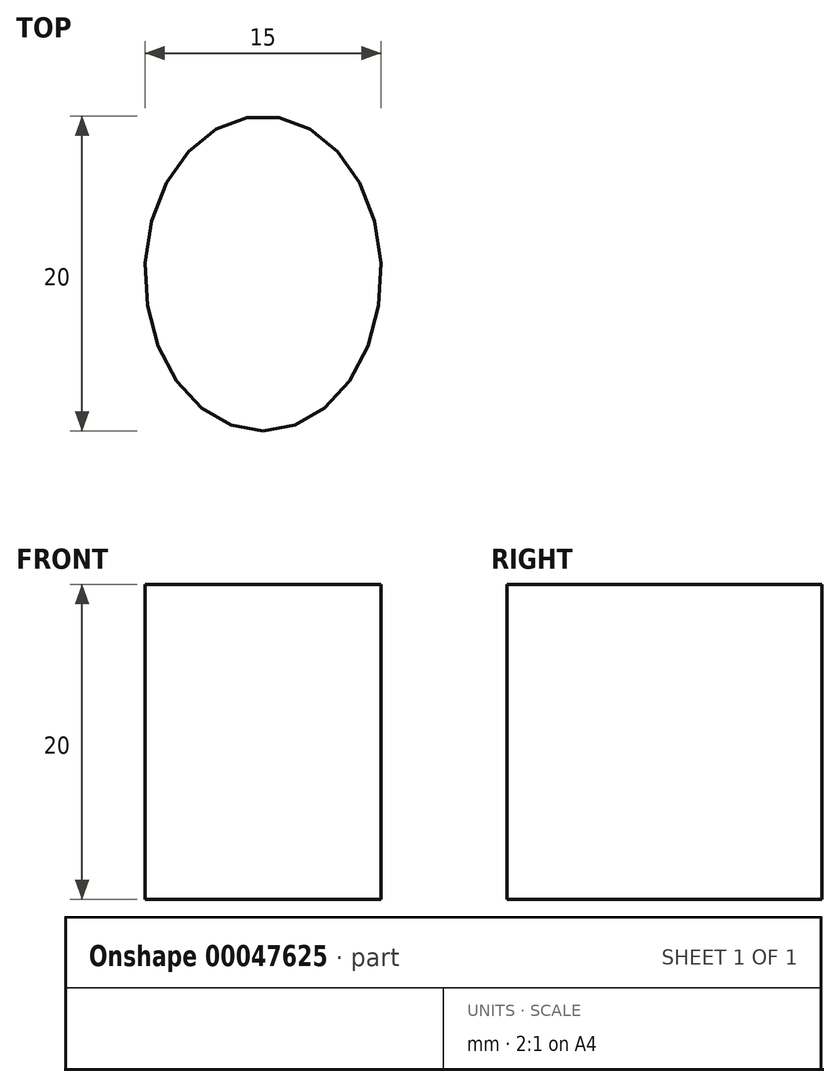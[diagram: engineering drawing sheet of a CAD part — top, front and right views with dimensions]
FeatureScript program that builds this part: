
annotation { "Feature Type Name" : "Feature", "Feature Type Description" : "" }
export const myFeature = defineFeature(function(context is Context, id is Id, definition is map)
    precondition{}
    {
        {
            var Q0;
            Q0=qCreatedBy(makeId("Top.planeOp"),FACE);
            var sketch = newSketch(context, id + "F0", { "sketchPlane" : qUnion([Q0])});
            skEllipse(sketch, "E0", {"center": v(-8.23, 16.06) * mm, "majorRadius": 10 * mm, "minorRadius": 7.5 * mm, "majorAxis": v(0, -1)});
            skSolve(sketch);
        }
        {
            var Q0;
            Q0=makeQuery(id+"F0.imprint","IMPRINT",FACE,{"disambiguationData":[TD([[makeQuery(id+"F0.imprint","IMPRINT",EDGE,{"derivedFrom":sQuery(id+"F0.wireOp",EDGE,"E0")}),1.0]])]});
            extrude(context, id + "F1", {"entities" : qUnion([Q0]), "depth" : 20 * mm});
        }
    });
